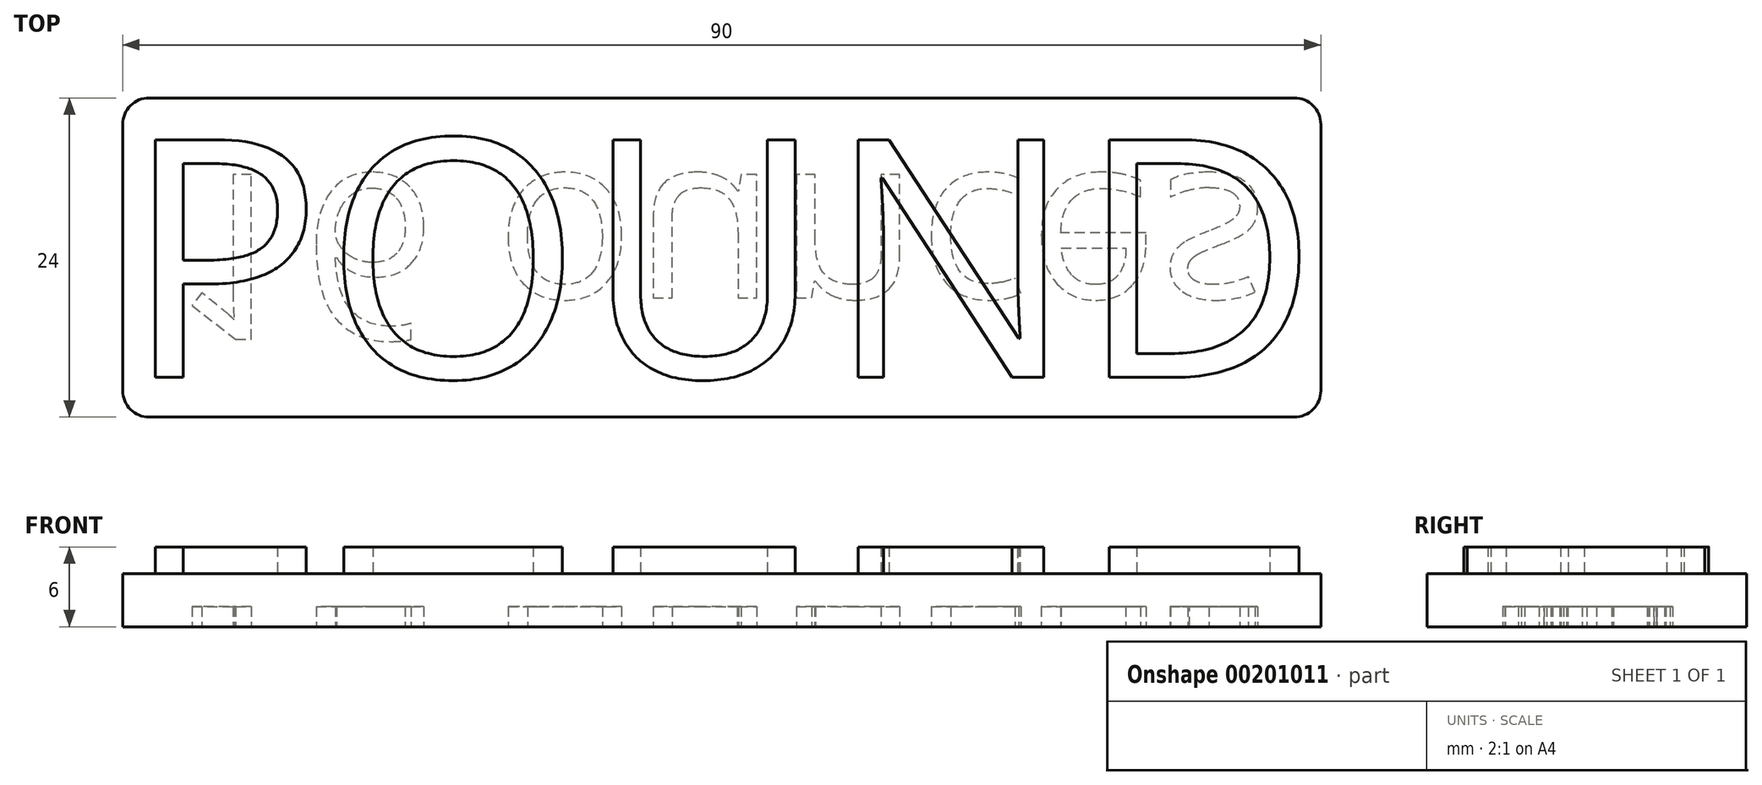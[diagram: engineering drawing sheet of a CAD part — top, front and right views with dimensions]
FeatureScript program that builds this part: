
annotation { "Feature Type Name" : "Feature", "Feature Type Description" : "" }
export const myFeature = defineFeature(function(context is Context, id is Id, definition is map)
    precondition{}
    {
        {
            var Q0;
            Q0=qCreatedBy(makeId("Top.planeOp"),FACE);
            var sketch = newSketch(context, id + "F0", { "sketchPlane" : qUnion([Q0])});
            skLineSegment(sketch, "E0.bottom", {"start": v(-45, 12) * mm, "end": v(45, 12) * mm});
            skLineSegment(sketch, "E0.top", {"start": v(-45, -12) * mm, "end": v(45, -12) * mm});
            skLineSegment(sketch, "E0.left", {"start": v(-45, 12) * mm, "end": v(-45, -12) * mm});
            skLineSegment(sketch, "E0.right", {"start": v(45, 12) * mm, "end": v(45, -12) * mm});
            skLineSegment(sketch, "E1", {"start": v(0, -12) * mm, "end": v(0, 12) * mm, "construction": true});
            skSolve(sketch);
        }
        {
            var Q0;
            Q0=makeQuery(id+"F0.imprint","IMPRINT",FACE,{"disambiguationData":[TD([[makeQuery(id+"F0.imprint","IMPRINT",EDGE,{"derivedFrom":sQuery(id+"F0.wireOp",EDGE,"E0.bottom")}),-1.0]])]});
            extrude(context, id + "F1", {"entities" : qUnion([Q0]), "depth" : 4 * mm});
        }
        {
            var Q0;
            Q0=makeQuery(id+"F1.opExtrude","SWEPT_EDGE",EDGE,{"disambiguationData":[OSD([sQuery(id+"F0.wireOp",EDGE,"E0.top"),sQuery(id+"F0.wireOp",EDGE,"E0.left")])]});
            var Q1;
            Q1=makeQuery(id+"F1.opExtrude","SWEPT_EDGE",EDGE,{"disambiguationData":[OSD([sQuery(id+"F0.wireOp",EDGE,"E0.bottom"),sQuery(id+"F0.wireOp",EDGE,"E0.right")])]});
            var Q2;
            Q2=makeQuery(id+"F1.opExtrude","SWEPT_EDGE",EDGE,{"disambiguationData":[OSD([sQuery(id+"F0.wireOp",EDGE,"E0.bottom"),sQuery(id+"F0.wireOp",EDGE,"E0.left")])]});
            var Q3;
            Q3=makeQuery(id+"F1.opExtrude","SWEPT_EDGE",EDGE,{"disambiguationData":[OSD([sQuery(id+"F0.wireOp",EDGE,"E0.top"),sQuery(id+"F0.wireOp",EDGE,"E0.right")])]});
            fillet(context, id + "F2", {"entities" : qUnion([Q0, Q1, Q2, Q3]), "radius" : 2 * mm, "tangentPropagation" : true, "allowEdgeOverflow" : false});
        }
        {
            var Q0;
            Q0=makeQuery(id+"F1.opExtrude","CAP_FACE",FACE,{"disambiguationData":[OSD([sQuery(id+"F0.wireOp",EDGE,"E0.bottom"),sQuery(id+"F0.wireOp",EDGE,"E0.top"),sQuery(id+"F0.wireOp",EDGE,"E0.left"),sQuery(id+"F0.wireOp",EDGE,"E0.right")])],"isStart":false});
            var sketch = newSketch(context, id + "F3", { "sketchPlane" : qUnion([Q0])});
            skText(sketch, "E2", { "text": "POUND", "fontName": "OpenSans-Regular.ttf"});
            const initialGuessF3  = {"E2": [-0.045, -0.00901, 1, 0, 0.01802]};
            skSetInitialGuess(sketch, initialGuessF3);
            skSolve(sketch);
        }
        {
            var Q0;
            {var subQ0=sQuery(id+"F3.wireOp",EDGE,"E2.sketch_text.stroke-4");Q0=makeQuery(id+"F3.imprint","IMPRINT",FACE,{"disambiguationData":[TD([[makeQuery(id+"F3.imprint","IMPRINT",EDGE,{"derivedFrom":subQ0}),-1.0]])]});}
            var Q1;
            {var subQ0=sQuery(id+"F3.wireOp",EDGE,"E2.sketch_text.stroke-3");var subQ1=sQuery(id+"F3.wireOp",EDGE,"E2.sketch_text.stroke-2");var subQ2=makeQuery(id+"F3.imprint","INTERSECT",VERTEX,{"derivedFrom":[subQ1,subQ0]});Q1=makeQuery(id+"F3.imprint","IMPRINT",FACE,{"disambiguationData":[TD([[makeQuery(id+"F3.imprint","IMPRINT",EDGE,{"disambiguationData":[TD([[subQ2,1.0]])],"derivedFrom":subQ1}),-1.0]])]});}
            var Q2;
            {var subQ1=sQuery(id+"F3.wireOp",EDGE,"E2.sketch_text.stroke-1");Q2=makeQuery(id+"F3.imprint","IMPRINT",FACE,{"disambiguationData":[TD([[makeQuery(id+"F3.imprint","IMPRINT",EDGE,{"derivedFrom":subQ1}),-1.0]])]});}
            var Q3;
            {var subQ0=sQuery(id+"F3.wireOp",EDGE,"E2.sketch_text.stroke-0");var subQ1=makeQuery(id+"F1.opExtrude","CAP_EDGE",EDGE,{"disambiguationData":[OSD([sQuery(id+"F0.wireOp",EDGE,"E0.top")])],"isStart":false});var subQ2=makeQuery(id+"F3.imprint","INTERSECT",VERTEX,{"derivedFrom":[subQ1,subQ0]});Q3=makeQuery(id+"F3.imprint","IMPRINT",FACE,{"disambiguationData":[TD([[makeQuery(id+"F3.imprint","IMPRINT",EDGE,{"disambiguationData":[TD([[subQ2,-1.0]])],"derivedFrom":subQ0}),-1.0]])]});}
            var Q4;
            {var subQ1=sQuery(id+"F3.wireOp",EDGE,"E2.sketch_text.stroke-8");Q4=makeQuery(id+"F3.imprint","IMPRINT",FACE,{"disambiguationData":[TD([[makeQuery(id+"F3.imprint","IMPRINT",EDGE,{"derivedFrom":subQ1}),-1.0]])]});}
            var Q5;
            {var subQ0=sQuery(id+"F3.wireOp",EDGE,"E2.sketch_text.stroke-9");var subQ1=makeQuery(id+"F1.opExtrude","CAP_EDGE",EDGE,{"disambiguationData":[OSD([sQuery(id+"F0.wireOp",EDGE,"E0.bottom")])],"isStart":false});var subQ2=makeQuery(id+"F3.imprint","INTERSECT",VERTEX,{"derivedFrom":[subQ1,subQ0]});Q5=makeQuery(id+"F3.imprint","IMPRINT",FACE,{"disambiguationData":[TD([[makeQuery(id+"F3.imprint","IMPRINT",EDGE,{"disambiguationData":[TD([[subQ2,1.0]])],"derivedFrom":subQ0}),-1.0]])]});}
            var Q6;
            {var subQ1=sQuery(id+"F3.wireOp",EDGE,"E2.sketch_text.stroke-10");Q6=makeQuery(id+"F3.imprint","IMPRINT",FACE,{"disambiguationData":[TD([[makeQuery(id+"F3.imprint","IMPRINT",EDGE,{"derivedFrom":subQ1}),-1.0]])]});}
            var Q7;
            {var subQ0=sQuery(id+"F3.wireOp",EDGE,"E2.sketch_text.stroke-11");var subQ1=makeQuery(id+"F1.opExtrude","CAP_EDGE",EDGE,{"disambiguationData":[OSD([sQuery(id+"F0.wireOp",EDGE,"E0.bottom")])],"isStart":false});var subQ2=makeQuery(id+"F3.imprint","INTERSECT",VERTEX,{"derivedFrom":[subQ1,subQ0]});Q7=makeQuery(id+"F3.imprint","IMPRINT",FACE,{"disambiguationData":[TD([[makeQuery(id+"F3.imprint","IMPRINT",EDGE,{"disambiguationData":[TD([[subQ2,-1.0]])],"derivedFrom":subQ0}),-1.0]])]});}
            var Q8;
            {var subQ0=sQuery(id+"F3.wireOp",EDGE,"E2.sketch_text.stroke-12");Q8=makeQuery(id+"F3.imprint","IMPRINT",FACE,{"disambiguationData":[TD([[makeQuery(id+"F3.imprint","IMPRINT",EDGE,{"derivedFrom":subQ0}),-1.0]])]});}
            var Q9;
            {var subQ0=sQuery(id+"F3.wireOp",EDGE,"E2.sketch_text.stroke-21");Q9=makeQuery(id+"F3.imprint","IMPRINT",FACE,{"disambiguationData":[TD([[makeQuery(id+"F3.imprint","IMPRINT",EDGE,{"derivedFrom":subQ0}),-1.0]])]});}
            var Q10;
            {var subQ0=sQuery(id+"F3.wireOp",EDGE,"E2.sketch_text.stroke-18");var subQ1=makeQuery(id+"F1.opExtrude","CAP_EDGE",EDGE,{"disambiguationData":[OSD([sQuery(id+"F0.wireOp",EDGE,"E0.top")])],"isStart":false});var subQ2=makeQuery(id+"F3.imprint","INTERSECT",VERTEX,{"derivedFrom":[subQ1,subQ0]});Q10=makeQuery(id+"F3.imprint","IMPRINT",FACE,{"disambiguationData":[TD([[makeQuery(id+"F3.imprint","IMPRINT",EDGE,{"disambiguationData":[TD([[subQ2,-1.0]])],"derivedFrom":subQ0}),-1.0]])]});}
            var Q11;
            {var subQ0=sQuery(id+"F3.wireOp",EDGE,"E2.sketch_text.stroke-19");Q11=makeQuery(id+"F3.imprint","IMPRINT",FACE,{"disambiguationData":[TD([[makeQuery(id+"F3.imprint","IMPRINT",EDGE,{"derivedFrom":subQ0}),-1.0]])]});}
            var Q12;
            {var subQ0=sQuery(id+"F3.wireOp",EDGE,"E2.sketch_text.stroke-25");Q12=makeQuery(id+"F3.imprint","IMPRINT",FACE,{"disambiguationData":[TD([[makeQuery(id+"F3.imprint","IMPRINT",EDGE,{"derivedFrom":subQ0}),-1.0]])]});}
            var Q13;
            {var subQ0=sQuery(id+"F3.wireOp",EDGE,"E2.sketch_text.stroke-22");var subQ1=makeQuery(id+"F1.opExtrude","CAP_EDGE",EDGE,{"disambiguationData":[OSD([sQuery(id+"F0.wireOp",EDGE,"E0.top")])],"isStart":false});var subQ2=makeQuery(id+"F3.imprint","INTERSECT",VERTEX,{"derivedFrom":[subQ1,subQ0]});Q13=makeQuery(id+"F3.imprint","IMPRINT",FACE,{"disambiguationData":[TD([[makeQuery(id+"F3.imprint","IMPRINT",EDGE,{"disambiguationData":[TD([[subQ2,-1.0]])],"derivedFrom":subQ0}),-1.0]])]});}
            var Q14;
            {var subQ0=sQuery(id+"F3.wireOp",EDGE,"E2.sketch_text.stroke-23");Q14=makeQuery(id+"F3.imprint","IMPRINT",FACE,{"disambiguationData":[TD([[makeQuery(id+"F3.imprint","IMPRINT",EDGE,{"derivedFrom":subQ0}),-1.0]])]});}
            var Q15;
            {var subQ5=sQuery(id+"F3.wireOp",EDGE,"E2.sketch_text.stroke-28");Q15=makeQuery(id+"F3.imprint","IMPRINT",FACE,{"disambiguationData":[TD([[makeQuery(id+"F3.imprint","IMPRINT",EDGE,{"derivedFrom":subQ5}),-1.0]])]});}
            var Q16;
            {var subQ0=sQuery(id+"F3.wireOp",EDGE,"E2.sketch_text.stroke-34");Q16=makeQuery(id+"F3.imprint","IMPRINT",FACE,{"disambiguationData":[TD([[makeQuery(id+"F3.imprint","IMPRINT",EDGE,{"derivedFrom":subQ0}),-1.0]])]});}
            var Q17;
            {var subQ0=sQuery(id+"F3.wireOp",EDGE,"E2.sketch_text.stroke-30");Q17=makeQuery(id+"F3.imprint","IMPRINT",FACE,{"disambiguationData":[TD([[makeQuery(id+"F3.imprint","IMPRINT",EDGE,{"derivedFrom":subQ0}),-1.0]])]});}
            var Q18;
            {var subQ0=sQuery(id+"F3.wireOp",EDGE,"E2.sketch_text.stroke-6");Q18=makeQuery(id+"F3.imprint","IMPRINT",FACE,{"disambiguationData":[TD([[makeQuery(id+"F3.imprint","IMPRINT",EDGE,{"derivedFrom":subQ0}),-1.0]])]});}
            var Q19;
            {var subQ0=sQuery(id+"F3.wireOp",EDGE,"E2.sketch_text.stroke-17");Q19=makeQuery(id+"F3.imprint","IMPRINT",FACE,{"disambiguationData":[TD([[makeQuery(id+"F3.imprint","IMPRINT",EDGE,{"derivedFrom":subQ0}),-1.0]])]});}
            var Q20;
            {var subQ0=sQuery(id+"F3.wireOp",EDGE,"E2.sketch_text.stroke-27");Q20=makeQuery(id+"F3.imprint","IMPRINT",FACE,{"disambiguationData":[TD([[makeQuery(id+"F3.imprint","IMPRINT",EDGE,{"derivedFrom":subQ0}),-1.0]])]});}
            var Q21;
            Q21=makeQuery(id+"F3.imprint","IMPRINT",FACE,{"disambiguationData":[TD([[makeQuery(id+"F3.imprint","IMPRINT",EDGE,{"derivedFrom":sQuery(id+"F3.wireOp",EDGE,"E2.sketch_text.stroke-45")}),-1.0]])]});
            var Q22;
            Q22=makeQuery(id+"F3.imprint","IMPRINT",FACE,{"disambiguationData":[TD([[makeQuery(id+"F3.imprint","IMPRINT",EDGE,{"derivedFrom":sQuery(id+"F3.wireOp",EDGE,"E2.sketch_text.stroke-60")}),-1.0]])]});
            extrude(context, id + "F4", {"entities" : qUnion([Q0, Q1, Q2, Q3, Q4, Q5, Q6, Q7, Q8, Q9, Q10, Q11, Q12, Q13, Q14, Q15, Q16, Q17, Q18, Q19, Q20, Q21, Q22]), "operationType" : NewBodyOperationType.ADD, "depth" : 2 * mm});
        }
        {
            var Q0;
            Q0=makeQuery(id+"F1.opExtrude","CAP_FACE",FACE,{"disambiguationData":[OSD([sQuery(id+"F0.wireOp",EDGE,"E0.bottom"),sQuery(id+"F0.wireOp",EDGE,"E0.top"),sQuery(id+"F0.wireOp",EDGE,"E0.left"),sQuery(id+"F0.wireOp",EDGE,"E0.right")])],"isStart":true});
            var sketch = newSketch(context, id + "F5", { "sketchPlane" : qUnion([Q0])});
            skText(sketch, "E3", { "text": "16 ounces", "fontName": "OpenSans-Regular.ttf"});
            const initialGuessF5  = {"E3": [-0.04139, -0.00625, 1, 0, 0.0125]};
            skSetInitialGuess(sketch, initialGuessF5);
            skSolve(sketch);
        }
        {
            var Q0;
            Q0=makeQuery(id+"F5.imprint","IMPRINT",FACE,{"disambiguationData":[TD([[makeQuery(id+"F5.imprint","IMPRINT",EDGE,{"derivedFrom":sQuery(id+"F5.wireOp",EDGE,"E3.sketch_text.stroke-141")}),-1.0]])]});
            var Q1;
            Q1=makeQuery(id+"F5.imprint","IMPRINT",FACE,{"disambiguationData":[TD([[makeQuery(id+"F5.imprint","IMPRINT",EDGE,{"derivedFrom":sQuery(id+"F5.wireOp",EDGE,"E3.sketch_text.stroke-122")}),-1.0]])]});
            var Q2;
            Q2=makeQuery(id+"F5.imprint","IMPRINT",FACE,{"disambiguationData":[TD([[makeQuery(id+"F5.imprint","IMPRINT",EDGE,{"derivedFrom":sQuery(id+"F5.wireOp",EDGE,"E3.sketch_text.stroke-103")}),-1.0]])]});
            var Q3;
            Q3=makeQuery(id+"F5.imprint","IMPRINT",FACE,{"disambiguationData":[TD([[makeQuery(id+"F5.imprint","IMPRINT",EDGE,{"derivedFrom":sQuery(id+"F5.wireOp",EDGE,"E3.sketch_text.stroke-86")}),-1.0]])]});
            var Q4;
            Q4=makeQuery(id+"F5.imprint","IMPRINT",FACE,{"disambiguationData":[TD([[makeQuery(id+"F5.imprint","IMPRINT",EDGE,{"derivedFrom":sQuery(id+"F5.wireOp",EDGE,"E3.sketch_text.stroke-70")}),-1.0]])]});
            var Q5;
            Q5=makeQuery(id+"F5.imprint","IMPRINT",FACE,{"disambiguationData":[TD([[makeQuery(id+"F5.imprint","IMPRINT",EDGE,{"derivedFrom":sQuery(id+"F5.wireOp",EDGE,"E3.sketch_text.stroke-39")}),-1.0]])]});
            var Q6;
            Q6=makeQuery(id+"F5.imprint","IMPRINT",FACE,{"disambiguationData":[TD([[makeQuery(id+"F5.imprint","IMPRINT",EDGE,{"derivedFrom":sQuery(id+"F5.wireOp",EDGE,"E3.sketch_text.stroke-19")}),-1.0]])]});
            var Q7;
            Q7=makeQuery(id+"F5.imprint","IMPRINT",FACE,{"disambiguationData":[TD([[makeQuery(id+"F5.imprint","IMPRINT",EDGE,{"derivedFrom":sQuery(id+"F5.wireOp",EDGE,"E3.sketch_text.stroke-0")}),-1.0]])]});
            var Q8;
            Q8=makeQuery(id+"F5.imprint","IMPRINT",FACE,{"disambiguationData":[TD([[makeQuery(id+"F5.imprint","IMPRINT",EDGE,{"derivedFrom":sQuery(id+"F5.wireOp",EDGE,"E3.sketch_text.stroke-51")}),-1.0]])]});
            extrude(context, id + "F6", {"entities" : qUnion([Q0, Q1, Q2, Q3, Q4, Q5, Q6, Q7, Q8]), "operationType" : NewBodyOperationType.REMOVE, "oppositeDirection" : true, "depth" : 1.5 * mm});
        }
    });
